# Revit family: Accessory-Shower_Bar-KOHLER-CHOREOGRAPH-K-97628
name_source: partatom
category: Specialty Equipment
units: mm (PartAtom-declared; Revit-internal decimal feet)

## family parameters
Cut with Voids When Loaded = No
Host = Face
OmniClass Number = 23.31.25.00
Part Type = Normal
Room Calculation Point = No
Round Connector Dimension = Use Diameter
Shared = No

## types (5) — shared parameters
ADA Compliant = No
Assembly Code = C1030200
Date Modified = 09/15/2024
Default Elevation = 42"
Description = 54 Ich Shower Barre
Height = 2 1/4"
Length = 54 1/4"
Manufacturer = Kohler Co.
Master Format 2014 = 10 28 00
Master Format 2014 Name = Toilet, Bath, and Laundry Accessories
Material = Anodized Aluminum
Product Documentation Link = https://www.us.kohler.com
Product Name = Choreograph
Product Page URL = http://www.us.kohler.com
URL = https://www.us.kohler.com
WaterSense Certified = No
Width = 3 1/2"

## per-type parameters (varying)
| type | Finish | Model | Type |
| SHP- Bright Polished Silver | Kohler-Metal-SHP-Bright_Polished_Silver | K-97628-SHP | 1 |
| ABZ- Anodized Dark Bronze | Kohler-Metal-ABZ-Anodized_Dark_Bronze | K-97628-ABZ | 2 |
| BNK- Anodized Brushed Nickel | Kohler-Metal-BNK-Anodized_Brushed_Nickel | K-97628-BNK | 3 |
| 2MB-Vibrant Brushed Moderne Brass | Kohler-Metal-2MB-Vibrant_Brushed_Moderne_Brass | K-97628-2MB | 4 |
| BL-Matte Black | Kohler-Metal-BL-Matte_Black | K-97628-BL | 5 |

## geometry (parser evidence)
native form markers: Sweep x4
no freeform markers — native parametric forms only
